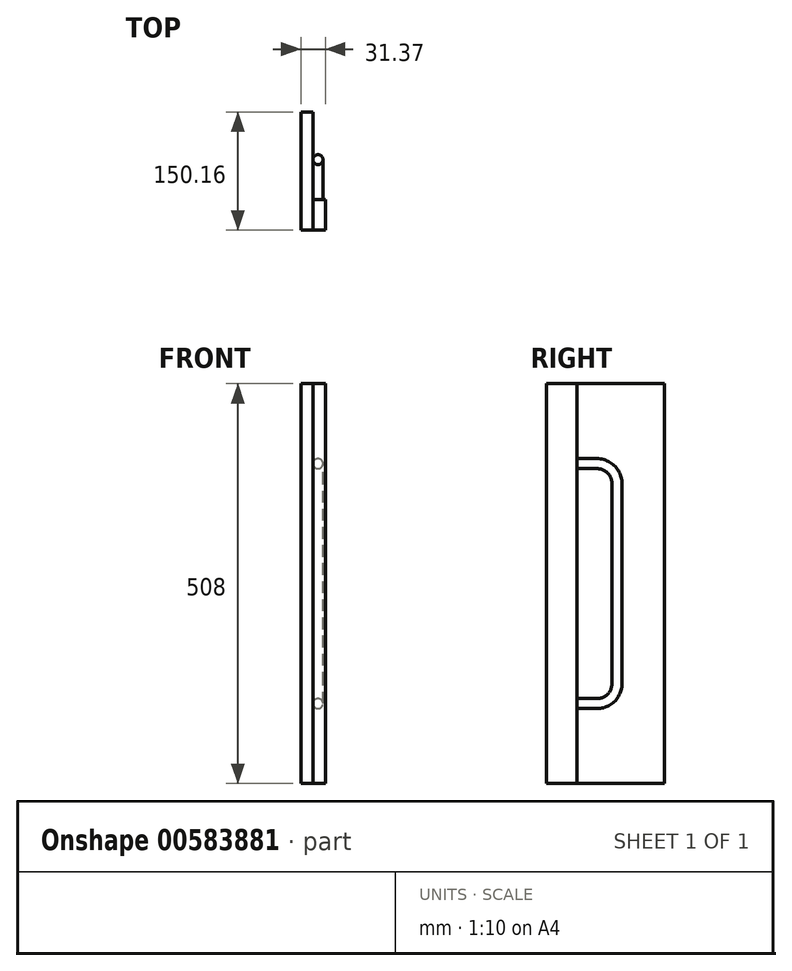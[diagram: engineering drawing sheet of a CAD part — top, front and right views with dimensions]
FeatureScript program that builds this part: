
annotation { "Feature Type Name" : "Feature", "Feature Type Description" : "" }
export const myFeature = defineFeature(function(context is Context, id is Id, definition is map)
    precondition{}
    {
        {
            var Q0;
            Q0=qCreatedBy(makeId("Right.planeOp"),FACE);
            var sketch = newSketch(context, id + "F0", { "sketchPlane" : qUnion([Q0])});
            skLineSegment(sketch, "E0.bottom", {"start": v(0, 152.4) * mm, "end": v(0, 152.4) * mm});
            skLineSegment(sketch, "E0.right", {"start": v(25.4, 127) * mm, "end": v(25.4, 0) * mm});
            skPoint(sketch, "E1.visualSharp", {"position": v(25.4, 152.4) * mm});
            skArc(sketch, "E1.filletArc", {"start": v(25.4, 127) * mm, "mid": v(17.96, 144.96) * mm, "end": v(0, 152.4) * mm});
            skLineSegment(sketch, "E2.MirrorCS", {"start": v(25.4, -127) * mm, "end": v(25.4, 0) * mm});
            skArc(sketch, "E3.MirrorCS", {"start": v(25.4, -127) * mm, "mid": v(17.96, -144.96) * mm, "end": v(0, -152.4) * mm});
            skLineSegment(sketch, "E4.top", {"start": v(-25.4, 152.4) * mm, "end": v(0, 152.4) * mm});
            skLineSegment(sketch, "E5.MirrorCS", {"start": v(-25.4, -152.4) * mm, "end": v(0, -152.4) * mm});
            skPoint(sketch, "E6.MirrorCS.end.orphan", {"position": v(-25.4, -152.4) * mm});
            skPoint(sketch, "E6.MirrorCS.start.orphan", {"position": v(-25.4, -127) * mm});
            skPoint(sketch, "E4.left.start.orphan", {"position": v(-25.4, 127) * mm});
            skSolve(sketch);
        }
        {
            var Q0;
            Q0=qCreatedBy(makeId("Top.planeOp"),FACE);
            var sketch = newSketch(context, id + "F1", { "sketchPlane" : qUnion([Q0])});
            skPoint(sketch, "E7.0", {"position": v(0, 25.4) * mm});
            skCircle(sketch, "E8", {"center": v(0, 25.4) * mm, "radius": 6.35 * mm});
            skSolve(sketch);
        }
        {
            var Q0;
            Q0=makeQuery(id+"F1.imprint","IMPRINT",FACE,{"disambiguationData":[TD([[makeQuery(id+"F1.imprint","IMPRINT",EDGE,{"derivedFrom":sQuery(id+"F1.wireOp",EDGE,"E8")}),1.0]])]});
            var Q1;
            Q1=sQuery(id+"F0.wireOp",EDGE,"E0.right");
            var Q2;
            Q2=sQuery(id+"F0.wireOp",EDGE,"E2.MirrorCS");
            var Q3;
            Q3=sQuery(id+"F0.wireOp",EDGE,"E3.MirrorCS");
            var Q4;
            Q4=sQuery(id+"F0.wireOp",EDGE,"E5.MirrorCS");
            var Q5;
            Q5=sQuery(id+"F0.wireOp",EDGE,"E1.filletArc");
            var Q6;
            Q6=sQuery(id+"F0.wireOp",EDGE,"E4.top");
            sweep(context, id + "F2", {"profiles" : qUnion([Q0]), "path" : qUnion([Q1, Q2, Q3, Q4, Q5, Q6])});
        }
        {
            var Q0;
            Q0=qCreatedBy(makeId("Top.planeOp"),FACE);
            var sketch = newSketch(context, id + "F3", { "sketchPlane" : qUnion([Q0])});
            skLineSegment(sketch, "E9.0", {"start": v(6.35, -25.4) * mm, "end": v(-6.35, -25.4) * mm});
            skLineSegment(sketch, "E10.bottom", {"start": v(-6.35, -25.4) * mm, "end": v(9.52, -25.4) * mm});
            skLineSegment(sketch, "E10.top", {"start": v(-6.35, -64.24) * mm, "end": v(9.53, -64.24) * mm});
            skLineSegment(sketch, "E10.left", {"start": v(-6.35, -25.4) * mm, "end": v(-6.35, -64.24) * mm});
            skLineSegment(sketch, "E10.right", {"start": v(9.52, -25.4) * mm, "end": v(9.53, -64.24) * mm});
            skSolve(sketch);
        }
        {
            var Q0;
            Q0=qCreatedBy(makeId("Top.planeOp"),FACE);
            var sketch = newSketch(context, id + "F4", { "sketchPlane" : qUnion([Q0])});
            skPoint(sketch, "E11.0", {"position": v(-6.35, -64.24) * mm});
            skLineSegment(sketch, "E12.bottom", {"start": v(-6.35, -64.24) * mm, "end": v(-21.84, -64.24) * mm});
            skLineSegment(sketch, "E12.top", {"start": v(-6.35, 85.92) * mm, "end": v(-21.84, 85.92) * mm});
            skLineSegment(sketch, "E12.left", {"start": v(-6.35, -64.24) * mm, "end": v(-6.35, 85.92) * mm});
            skLineSegment(sketch, "E12.right", {"start": v(-21.84, -64.24) * mm, "end": v(-21.84, 85.92) * mm});
            skSolve(sketch);
        }
        {
            var Q0;
            Q0=makeQuery(id+"F3.imprint","IMPRINT",FACE,{"disambiguationData":[TD([[makeQuery(id+"F3.imprint","IMPRINT",EDGE,{"derivedFrom":sQuery(id+"F3.wireOp",EDGE,"E10.top")}),1.0]])]});
            extrude(context, id + "F5", {"entities" : qUnion([Q0]), "endBound" : BoundingType.SYMMETRIC, "depth" : 508 * mm, "offsetDistance" : 25.4 * mm});
        }
        {
            var Q0;
            Q0=makeQuery(id+"F4.imprint","IMPRINT",FACE,{"disambiguationData":[TD([[makeQuery(id+"F4.imprint","IMPRINT",EDGE,{"derivedFrom":sQuery(id+"F4.wireOp",EDGE,"E12.bottom")}),-1.0]])]});
            extrude(context, id + "F6", {"entities" : qUnion([Q0]), "endBound" : BoundingType.SYMMETRIC, "depth" : 508 * mm, "offsetDistance" : 25.4 * mm});
        }
    });
